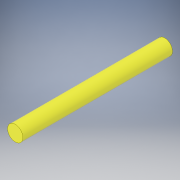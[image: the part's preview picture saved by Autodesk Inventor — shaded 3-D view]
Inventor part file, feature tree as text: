
AUTODESK INVENTOR PART (.ipt)
format: ipt  version: 2019 (Build 230136000, 136)  size: 91,648 bytes
history: native  units: mm
features: extrude x1, sketch x1
ambient origin geometry x8: Origin, YZ Plane, XZ Plane, XY Plane, X Axis, Y Axis, Z Axis, Center Point
bodies: Solid1 (feature_tree)
feature tree (2):
  extrude  "Extrusion1"  Depth=34.0mm TaperAngle=0.0deg
  sketch  "Sketch1"  dims[d0=3.5mm d1=34.0mm d2=0.0mm]
